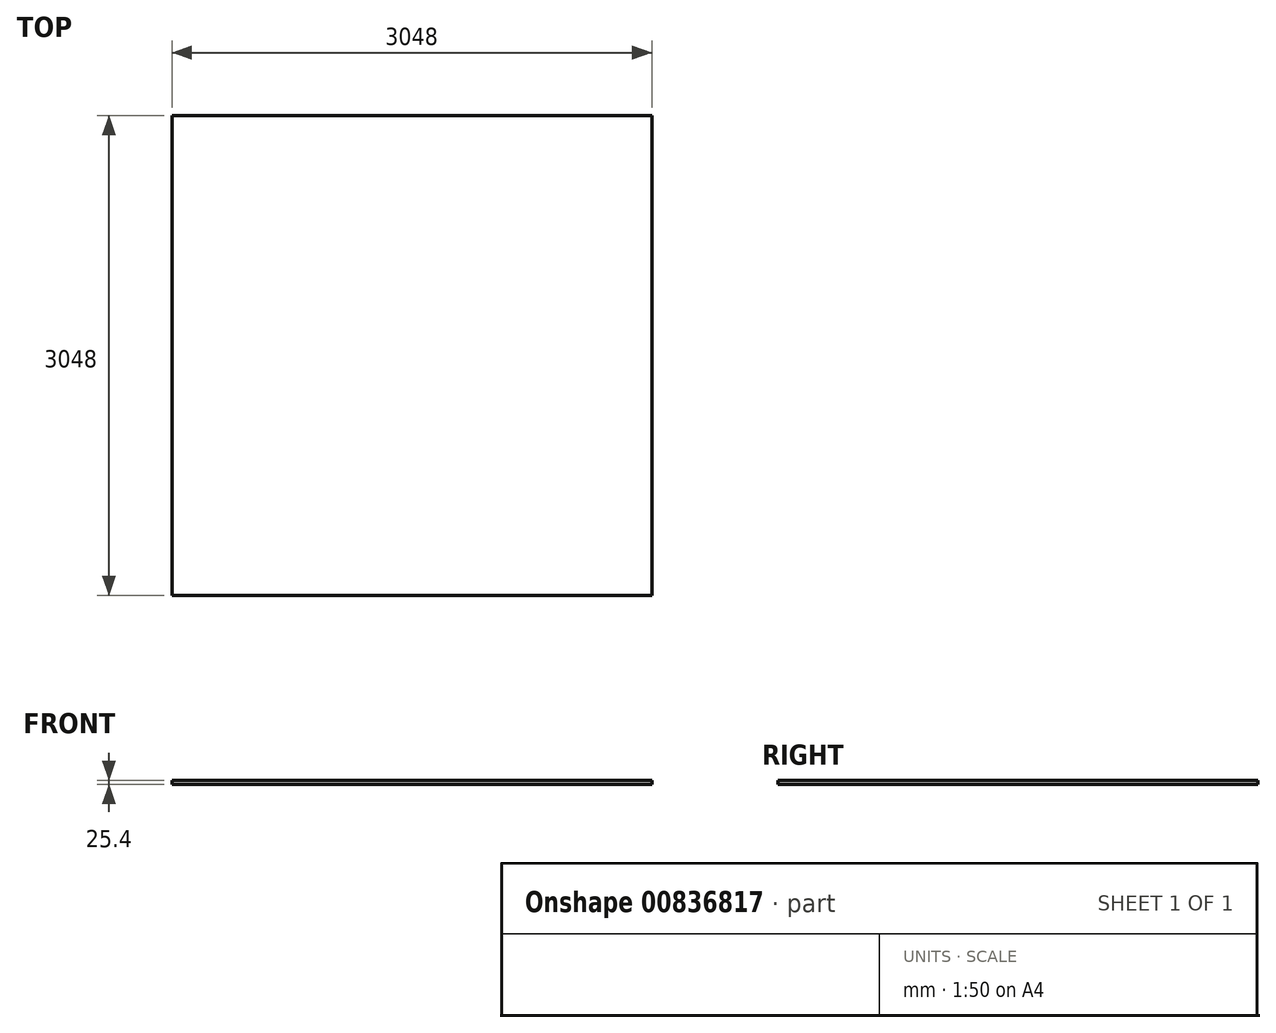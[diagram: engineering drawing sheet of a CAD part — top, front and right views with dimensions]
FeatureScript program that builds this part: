
annotation { "Feature Type Name" : "Feature", "Feature Type Description" : "" }
export const myFeature = defineFeature(function(context is Context, id is Id, definition is map)
    precondition{}
    {
        {
            var Q0;
            Q0=qCreatedBy(makeId("Top.planeOp"),FACE);
            var sketch = newSketch(context, id + "F0", { "sketchPlane" : qUnion([Q0])});
            skLineSegment(sketch, "E0.bottom", {"start": v(-1515.08, 2434.33) * mm, "end": v(1532.92, 2434.33) * mm});
            skLineSegment(sketch, "E0.top", {"start": v(-1515.08, -613.67) * mm, "end": v(1532.92, -613.67) * mm});
            skLineSegment(sketch, "E0.left", {"start": v(-1515.08, 2434.33) * mm, "end": v(-1515.08, -613.67) * mm});
            skLineSegment(sketch, "E0.right", {"start": v(1532.92, 2434.33) * mm, "end": v(1532.92, -613.67) * mm});
            skSolve(sketch);
        }
        {
            var Q0;
            Q0 = qSketchRegion(id + "F0", true);
            extrude(context, id + "F1", {"entities" : qUnion([Q0]), "depth" : 25.4 * mm, "offsetDistance" : 25.4 * mm});
        }
    });
